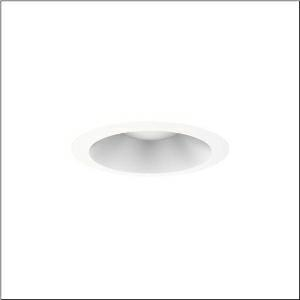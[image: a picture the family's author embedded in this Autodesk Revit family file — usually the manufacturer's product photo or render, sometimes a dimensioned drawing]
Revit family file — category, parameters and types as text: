
# Revit family: lunis_31-xl_51dn16eg42b
name_source: partatom
category: Lighting Fixtures
units: mm (PartAtom-declared; Revit-internal decimal feet)

## family parameters
Cut with Voids When Loaded = No
Host = Face
Light Source = No
Part Type = Normal
Room Calculation Point = No
Round Connector Dimension = Use Diameter
Shared = No

## types (1)
- --- (1 x LED, 2550 lm, 17 W, 4000K)
    Apparent Load = 17 VA
    CIE Flux Codes = 64 93 99 100 100
    Color Rendering = 80
    Color Temperature = 4000K
    Default Elevation = 1800 mm
    Description = Lunis 31, -XL, downlight, light control with reflector, light emission: direct distribution, LED rated luminous flux: 2.550lm, light colour: 840, mains connection: 220..240V, AC/DC, 0/50..60Hz, housing, of aluminium, white, protection rating (complete): IP20, protection rating (on room side): IP54, insulation class (complete): insulation class II (safety insulation), certification: CE, ENEC, packaging unit: 1 piece
    Height = 0 mm  [stored 0 ft]
    Lamp = 1 x LED
    Lamp Light Flux = 2550 lm
    Lamp Power = 17 W
    Lamp count = 1
    Length = 259 mm
    Luminous efficacy = 150 lm/W
    Manufacturer = Siteco
    ModVariant = No
    Model = 51DN16EG42B
    Mounting Place = Ceiling
    Mounting Type = Recessed
    Number of Poles = 1
    OnlyDefault = Yes
    Power Factor = 1
    Product Name = Lunis 31-XL
    Product group = downlight
    ProductGroupID = 401
    Protection Class = Protection class II
    Protection Degree = IP 20
    RLX_Detail_Level = 1
    RLX_Emergency_Light_Flux = 0 lm
    RLX_Emergency_Type = 0
    RLX_Emergency_Type_DB = No
    RlxData = <blob elided: 24149 chars, md5=72c889b6>
    Socket = socket
    Standby Power = 0 W
    System Light Flux = 2550 lm
    System Power = 17 W
    Type Comments = individual setting: luminous flux: 100 % | (ON | OFF | ON) | 450 mA
    Type Image = l_1345915.jpg
    URL = http://relux.com
    VarID = @adj_029719
    Voltage = 0 V
    Weight = 0.00 kg
    Width = 0 mm  [stored 0 ft]

note: [stored X ft] marks values corroborated as IEEE doubles in the binary element streams (Revit-internal decimal feet)

## geometry (parser evidence)
native form markers: Blend x4, Sweep x12
no freeform markers — native parametric forms only
